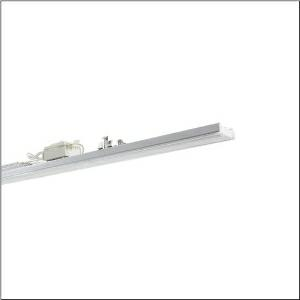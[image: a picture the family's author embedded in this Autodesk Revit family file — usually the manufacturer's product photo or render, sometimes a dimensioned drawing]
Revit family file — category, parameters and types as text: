
# Revit family: licross_r__11_recessed_mo_51te11mn4axg_8329
name_source: partatom
category: Lighting Fixtures
units: mm (PartAtom-declared; Revit-internal decimal feet)

## family parameters
Cut with Voids When Loaded = No
Host = Face
Light Source = No
Part Type = Normal
Room Calculation Point = No
Round Connector Dimension = Use Diameter
Shared = No

## types (1)
- --- (1 x LED, 10130 lm, 55.2 W, 4000K)
    Apparent Load = 55 VA
    CIE Flux Codes = 89 96 99 100 100
    Color Rendering = 80
    Color Temperature = 4000K
    Default Elevation = 1800 mm
    Description = Licross® 11 Recessed MO, luminaire insert, of sheet steel, galvanised, coil coated, white, length: 1.500mm, width: 66mm, height: 67mm, LED rated luminous flux: 10.130lm, light colour: 840, control gear: ON/OFF Multilumen, with plug, 3-pole, with phase selection, mains connection: 220..240V, AC, 50/60Hz, rated input power: 55W, internal wiring halogen-free, primary light control with lens, of plastic, primary optical cover: cover, of PMMA, light emission: direct distribution, primary light characteristic: symmetric, protection rating (complete): IP54, insulation class (complete): insulation class I (protective earthing), certification: CE, ENEC, VDE, UKCA, protection symbol: D if used in an environment with non-conductive dust loads with corresponding accessories, impact resistance: IK06, permissible ambient temperature for indoor applications: -35..+40°C, corresponds to IFS (International Featured Standards) requirements for safety and quality in the food industry, reducing of maximum allowable ambient temperature of 5°C with ceiling mounting, packaging unit: 1 piece
    Height = 58 mm
    Lamp = 1 x LED
    Lamp Light Flux = 10130 lm
    Lamp Power = 55.2 W
    Lamp count = 1
    Length = 1500 mm
    Luminous efficacy = 184 lm/W
    Manufacturer = Siteco
    ModVariant = No
    Model = 51TE11MN4AXG
    Mounting Place = Ceiling
    Mounting Type = Pendant
    Number of Poles = 1
    OnlyDefault = Yes
    Power Factor = 1
    Product Name = Licross® 11 Recessed MO
    Product group = luminaire insert | ceiling pendant
    ProductGroupID = 902
    Protection Class = Protection class I
    Protection Degree = IP 54
    RLX_Detail_Level = 1
    RLX_Emergency_Light_Flux = 0 lm
    RLX_Emergency_Type = 0
    RLX_Emergency_Type_DB = No
    RlxData = <blob elided: 22181 chars, md5=38755ac3>
    Socket = socket
    Standby Power = 0 W
    System Light Flux = 10130 lm
    System Power = 55 W
    Type Comments = factory setting: luminous flux: 100 % | (A | C | E) | 126 mA
    Type Image = l_1296930.jpg
    URL = http://relux.com
    VarID = @adj_106001
    Voltage = 0 V
    Weight = 0.00 kg
    Width = 66 mm

## geometry (parser evidence)
native form markers: Blend x4, Sweep x13
no freeform markers — native parametric forms only
